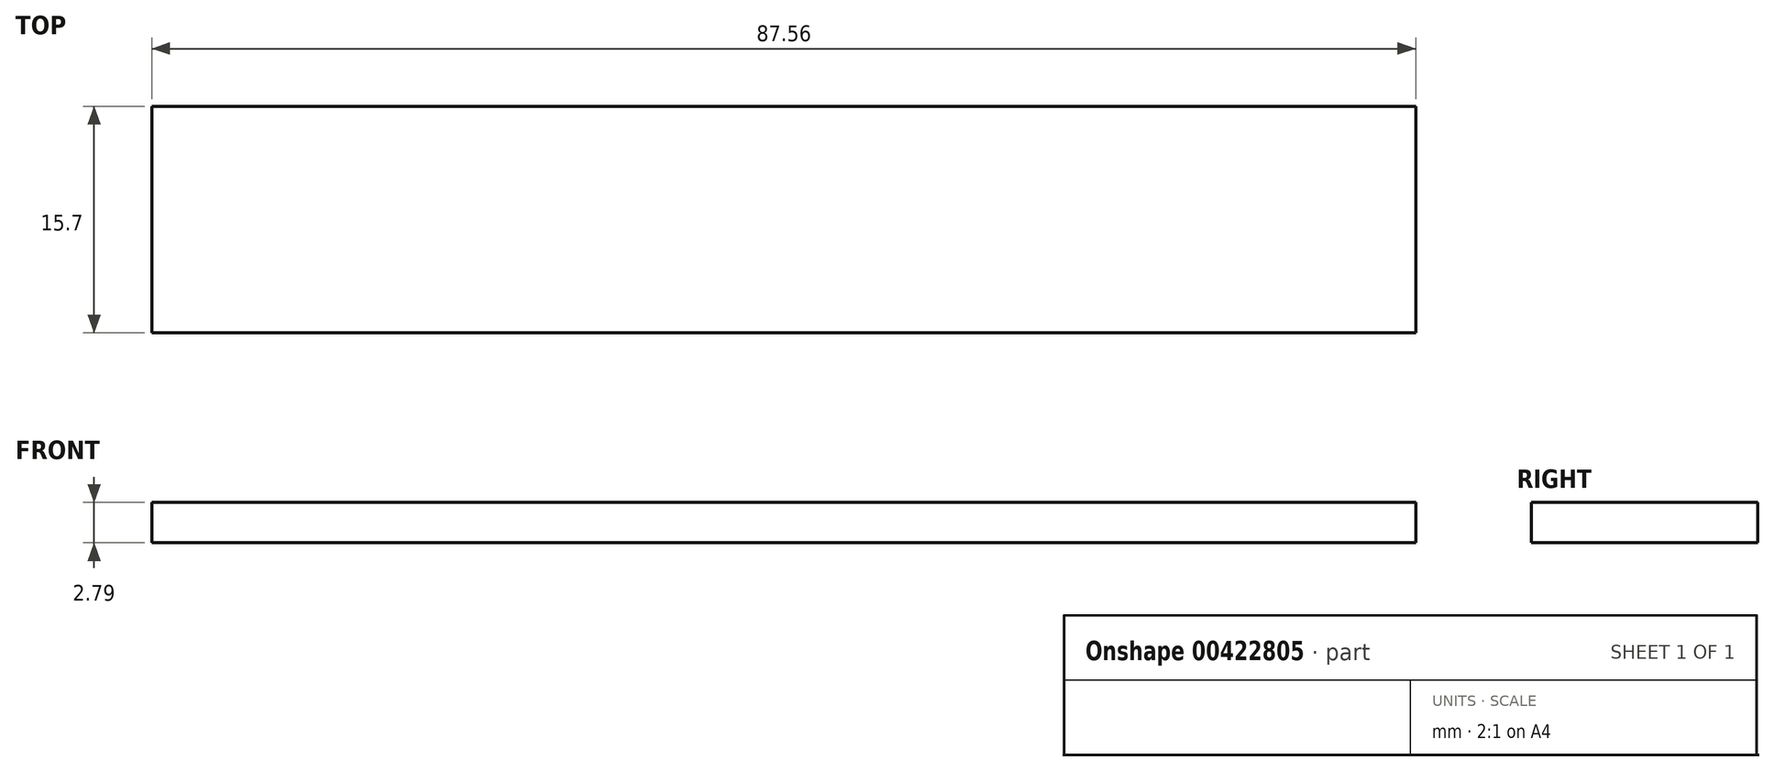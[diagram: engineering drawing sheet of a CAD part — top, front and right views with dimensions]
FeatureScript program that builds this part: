
annotation { "Feature Type Name" : "Feature", "Feature Type Description" : "" }
export const myFeature = defineFeature(function(context is Context, id is Id, definition is map)
    precondition{}
    {
        {
            var Q0;
            Q0=qCreatedBy(makeId("Top.planeOp"),FACE);
            var sketch = newSketch(context, id + "F0", { "sketchPlane" : qUnion([Q0])});
            skLineSegment(sketch, "E0.bottom", {"start": v(-41.67, 7.55) * mm, "end": v(45.9, 7.55) * mm});
            skLineSegment(sketch, "E0.top", {"start": v(-41.67, -8.15) * mm, "end": v(45.9, -8.15) * mm});
            skLineSegment(sketch, "E0.left", {"start": v(-41.67, 7.55) * mm, "end": v(-41.67, -8.15) * mm});
            skLineSegment(sketch, "E0.right", {"start": v(45.9, 7.55) * mm, "end": v(45.9, -8.15) * mm});
            skSolve(sketch);
        }
        {
            var Q0;
            Q0=makeQuery(id+"F0.imprint","IMPRINT",FACE,{"disambiguationData":[TD([[makeQuery(id+"F0.imprint","IMPRINT",EDGE,{"derivedFrom":sQuery(id+"F0.wireOp",EDGE,"E0.bottom")}),-1.0]])]});
            extrude(context, id + "F1", {"entities" : qUnion([Q0]), "depth" : 2.8 * mm});
        }
    });
